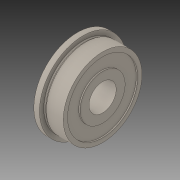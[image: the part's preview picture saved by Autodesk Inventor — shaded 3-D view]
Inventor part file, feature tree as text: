
AUTODESK INVENTOR PART (.ipt)
format: ipt  version: 2019 (Build 230136000, 136)  size: 148,480 bytes
history: native  units: in
note: dims shown in document units (in); Inventor stores cm internally (conversion verified against a paired STEP export)
features: revolve x1
ambient origin geometry x8: Origin, YZ Plane, XZ Plane, XY Plane, X Axis, Y Axis, Z Axis, Center Point
bodies: Solid1 (feature_tree)
feature tree (1):
  revolve  "Revolve1"  [1 undecoded]
note: 1 required parameter value undecoded (feature->parameter linkage not recoverable at this tier; creation-order binding heuristic only, values carry confidence <= 0.55)
